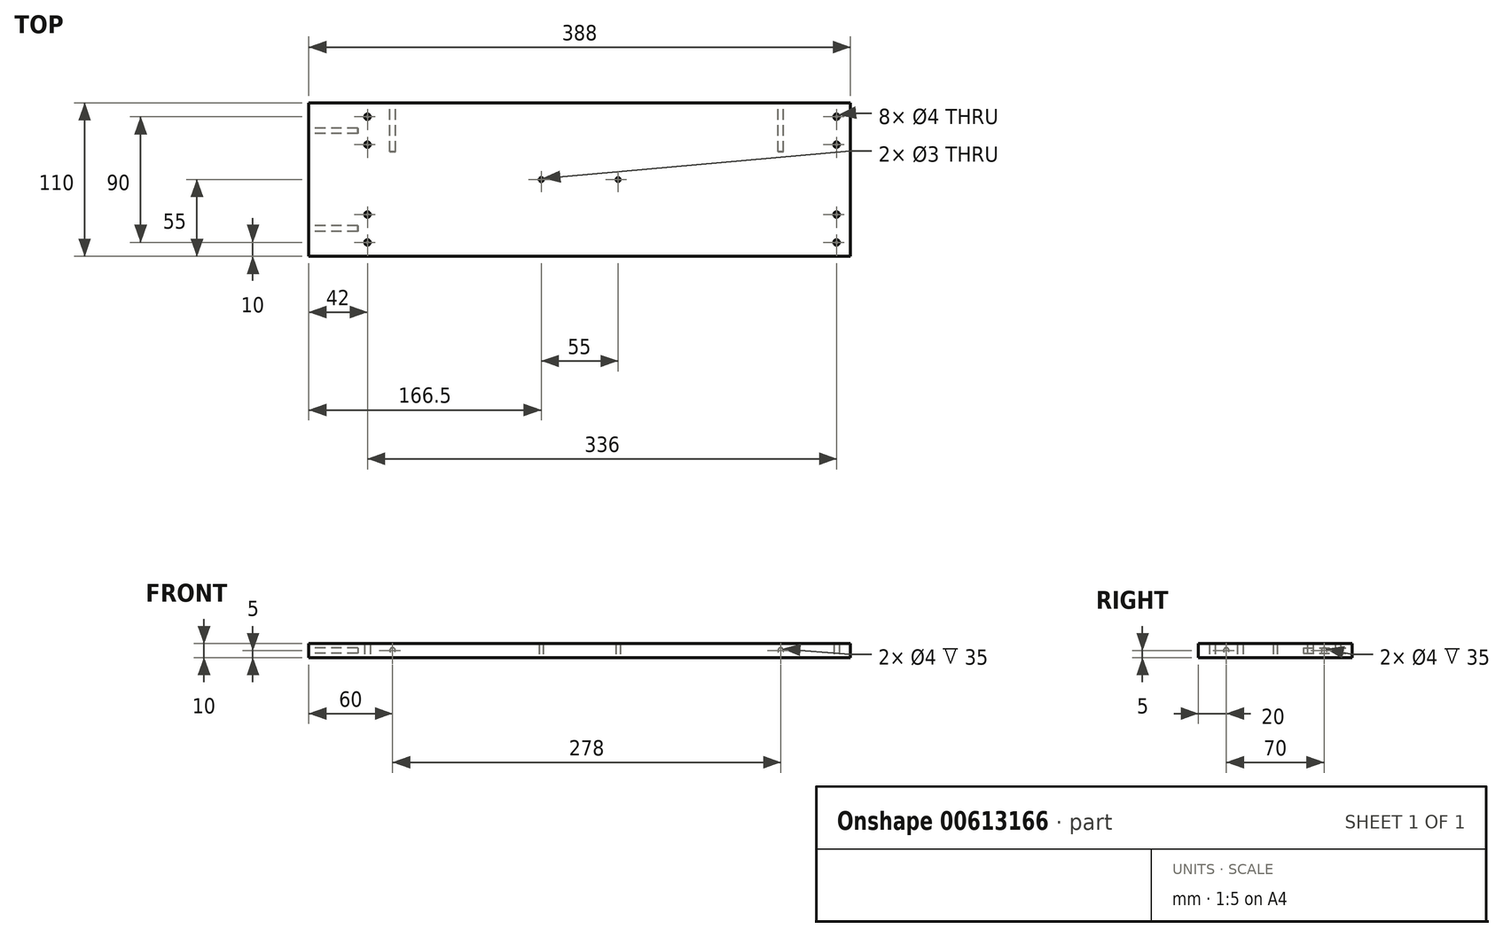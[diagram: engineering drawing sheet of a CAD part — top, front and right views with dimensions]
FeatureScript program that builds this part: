
annotation { "Feature Type Name" : "Feature", "Feature Type Description" : "" }
export const myFeature = defineFeature(function(context is Context, id is Id, definition is map)
    precondition{}
    {
        {
            var Q0;
            Q0=qCreatedBy(makeId("Top.planeOp"),FACE);
            var sketch = newSketch(context, id + "F0", { "sketchPlane" : qUnion([Q0])});
            skLineSegment(sketch, "E0.bottom", {"start": v(194, 55) * mm, "end": v(-194, 55) * mm});
            skLineSegment(sketch, "E0.top", {"start": v(194, -55) * mm, "end": v(-194, -55) * mm});
            skLineSegment(sketch, "E0.left", {"start": v(194, 55) * mm, "end": v(194, -55) * mm});
            skLineSegment(sketch, "E0.right", {"start": v(-194, 55) * mm, "end": v(-194, -55) * mm});
            skPoint(sketch, "E0.middle", {"position": v(0, 0) * mm});
            skLineSegment(sketch, "E1", {"start": v(184, 35) * mm, "end": v(184, -35) * mm, "construction": true});
            skPoint(sketch, "E2", {"position": v(184, 0) * mm});
            skLineSegment(sketch, "E3", {"start": v(-152, 35) * mm, "end": v(-152, -35) * mm, "construction": true});
            skPoint(sketch, "E4", {"position": v(-152, 0) * mm});
            skCircle(sketch, "E5", {"center": v(-27.5, 0) * mm, "radius": 1.5 * mm});
            skCircle(sketch, "E6", {"center": v(27.5, 0) * mm, "radius": 1.5 * mm});
            skLineSegment(sketch, "E7", {"start": v(-27.5, 0) * mm, "end": v(27.5, 0) * mm, "construction": true});
            skLineSegment(sketch, "E8", {"start": v(-152, 0) * mm, "end": v(184, 0) * mm, "construction": true});
            skCircle(sketch, "E9", {"center": v(184, -45) * mm, "radius": 2 * mm});
            skCircle(sketch, "E10", {"center": v(184, -25) * mm, "radius": 2 * mm});
            skCircle(sketch, "E11", {"center": v(-152, -45) * mm, "radius": 2 * mm});
            skCircle(sketch, "E12", {"center": v(-152, -25) * mm, "radius": 2 * mm});
            skCircle(sketch, "E13.MirrorC", {"center": v(184, 25) * mm, "radius": 2 * mm});
            skCircle(sketch, "E14.MirrorC", {"center": v(184, 45) * mm, "radius": 2 * mm});
            skCircle(sketch, "E15.MirrorC", {"center": v(-152, 45) * mm, "radius": 2 * mm});
            skCircle(sketch, "E16.MirrorC", {"center": v(-152, 25) * mm, "radius": 2 * mm});
            skSolve(sketch);
        }
        {
            var Q0;
            Q0=makeQuery(id+"F0.imprint","IMPRINT",FACE,{"disambiguationData":[TD([[makeQuery(id+"F0.imprint","IMPRINT",EDGE,{"derivedFrom":sQuery(id+"F0.wireOp",EDGE,"E0.bottom")}),1.0]])]});
            extrude(context, id + "F1", {"entities" : qUnion([Q0]), "depth" : 10 * mm, "offsetDistance" : 25 * mm});
        }
        {
            var Q0;
            Q0=makeQuery(id+"F1.opExtrude","SWEPT_FACE",FACE,{"disambiguationData":[OSD([sQuery(id+"F0.wireOp",EDGE,"E0.bottom")])]});
            var sketch = newSketch(context, id + "F2", { "sketchPlane" : qUnion([Q0])});
            skCircle(sketch, "E17", {"center": v(-144, 5) * mm, "radius": 2 * mm});
            skCircle(sketch, "E18", {"center": v(134, 5) * mm, "radius": 2 * mm});
            skSolve(sketch);
        }
        {
            var Q0;
            Q0=qSketchRegion(id+"F2",true);
            extrude(context, id + "F3", {"entities" : qUnion([Q0]), "operationType" : NewBodyOperationType.REMOVE, "oppositeDirection" : true, "depth" : 35 * mm, "offsetDistance" : 25 * mm});
        }
        {
            var Q0;
            Q0=makeQuery(id+"F1.opExtrude","SWEPT_FACE",FACE,{"disambiguationData":[OSD([sQuery(id+"F0.wireOp",EDGE,"E0.right")])]});
            var sketch = newSketch(context, id + "F4", { "sketchPlane" : qUnion([Q0])});
            skCircle(sketch, "E19", {"center": v(-35, 5) * mm, "radius": 2 * mm});
            skCircle(sketch, "E20", {"center": v(35, 5) * mm, "radius": 2 * mm});
            skSolve(sketch);
        }
        {
            var Q0;
            Q0=qSketchRegion(id+"F4",true);
            extrude(context, id + "F5", {"entities" : qUnion([Q0]), "operationType" : NewBodyOperationType.REMOVE, "oppositeDirection" : true, "depth" : 35 * mm, "offsetDistance" : 25 * mm});
        }
    });
